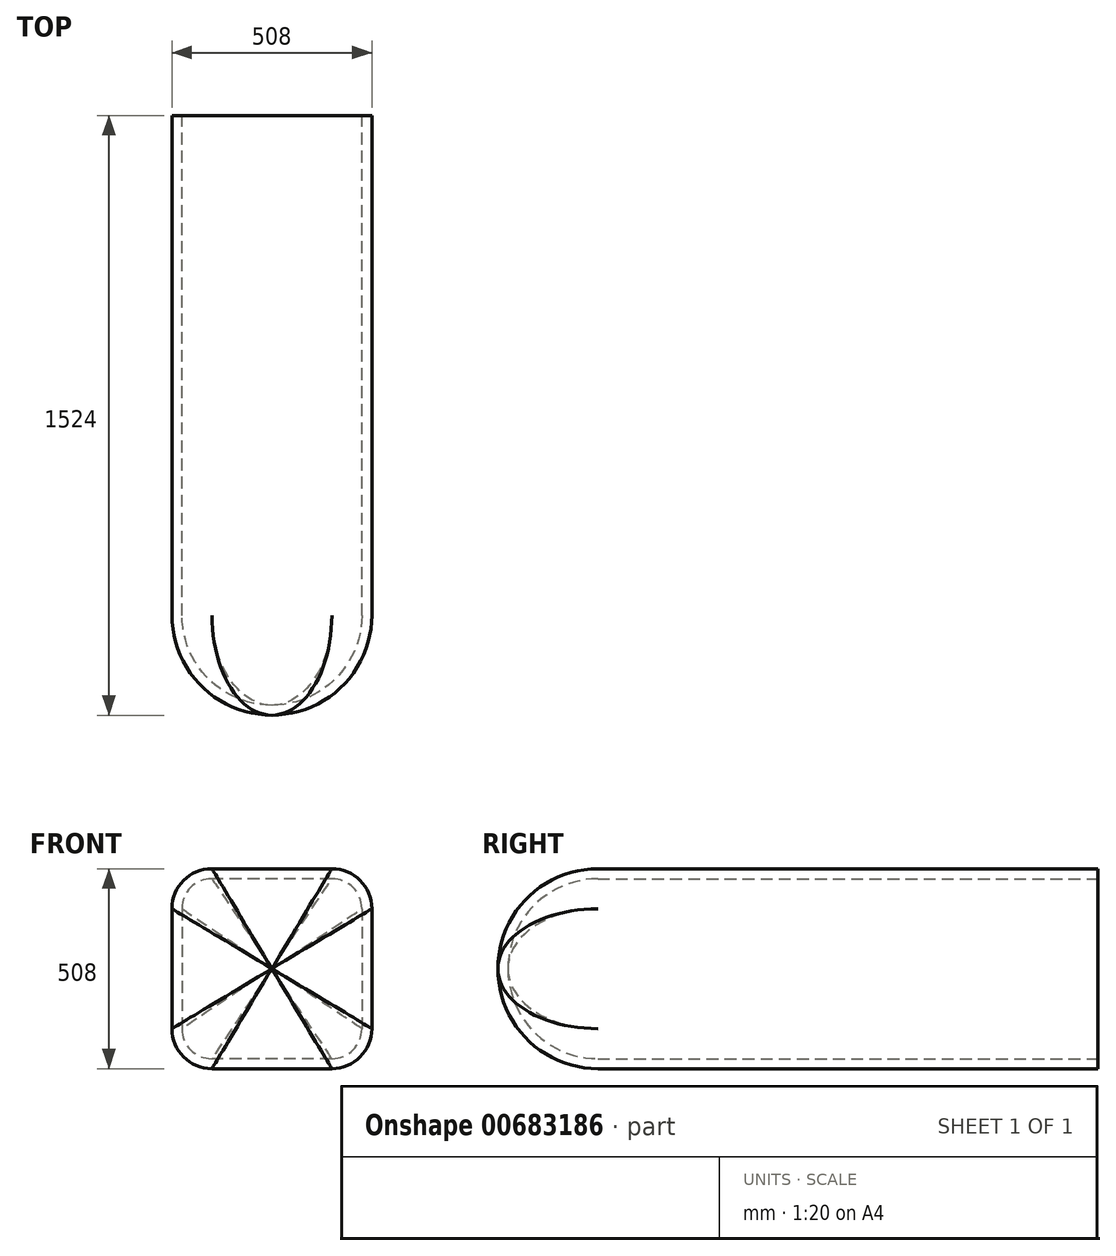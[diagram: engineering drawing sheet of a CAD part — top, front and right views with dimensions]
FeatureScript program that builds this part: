
annotation { "Feature Type Name" : "Feature", "Feature Type Description" : "" }
export const myFeature = defineFeature(function(context is Context, id is Id, definition is map)
    precondition{}
    {
        {
            var Q0;
            Q0=qCreatedBy(makeId("Right.planeOp"),FACE);
            var sketch = newSketch(context, id + "F0", { "sketchPlane" : qUnion([Q0])});
            skLineSegment(sketch, "E0.bottom", {"start": v(-1935.95, 401.63) * mm, "end": v(-411.95, 401.63) * mm});
            skLineSegment(sketch, "E0.top", {"start": v(-1935.95, -106.37) * mm, "end": v(-411.95, -106.37) * mm});
            skLineSegment(sketch, "E0.left", {"start": v(-1935.95, 401.63) * mm, "end": v(-1935.95, -106.37) * mm});
            skLineSegment(sketch, "E0.right", {"start": v(-411.95, 401.63) * mm, "end": v(-411.95, -106.37) * mm});
            skSolve(sketch);
        }
        {
            var Q0;
            Q0 = qSketchRegion(id + "F0", true);
            extrude(context, id + "F1", {"entities" : qUnion([Q0]), "depth" : 508 * mm, "offsetDistance" : 25.4 * mm});
        }
        {
            var Q0;
            Q0=makeQuery(id+"F1.opExtrude","CAP_EDGE",EDGE,{"disambiguationData":[OSD([sQuery(id+"F0.wireOp",EDGE,"E0.bottom")])],"isStart":false});
            var Q1;
            Q1=makeQuery(id+"F1.opExtrude","CAP_EDGE",EDGE,{"disambiguationData":[OSD([sQuery(id+"F0.wireOp",EDGE,"E0.top")])],"isStart":false});
            var Q2;
            Q2=makeQuery(id+"F1.opExtrude","CAP_EDGE",EDGE,{"disambiguationData":[OSD([sQuery(id+"F0.wireOp",EDGE,"E0.top")])],"isStart":true});
            var Q3;
            Q3=makeQuery(id+"F1.opExtrude","CAP_EDGE",EDGE,{"disambiguationData":[OSD([sQuery(id+"F0.wireOp",EDGE,"E0.bottom")])],"isStart":true});
            fillet(context, id + "F2", {"entities" : qUnion([Q0, Q1, Q2, Q3]), "radius" : 101.6 * mm, "tangentPropagation" : true, "allowEdgeOverflow" : false});
        }
        {
            var Q0;
            Q0=makeQuery(id+"F1.opExtrude","CAP_EDGE",EDGE,{"disambiguationData":[OSD([sQuery(id+"F0.wireOp",EDGE,"E0.left")])],"isStart":false});
            fillet(context, id + "F3", {"entities" : qUnion([Q0]), "radius" : 254 * mm, "tangentPropagation" : true, "allowEdgeOverflow" : false});
        }
        {
            var Q0;
            Q0=makeQuery(id+"F1.opExtrude","SWEPT_FACE",FACE,{"disambiguationData":[OSD([sQuery(id+"F0.wireOp",EDGE,"E0.right")])]});
            shell(context, id + "F4", {"entities" : qUnion([Q0]), "thickness" : 25.4 * mm});
        }
    });
